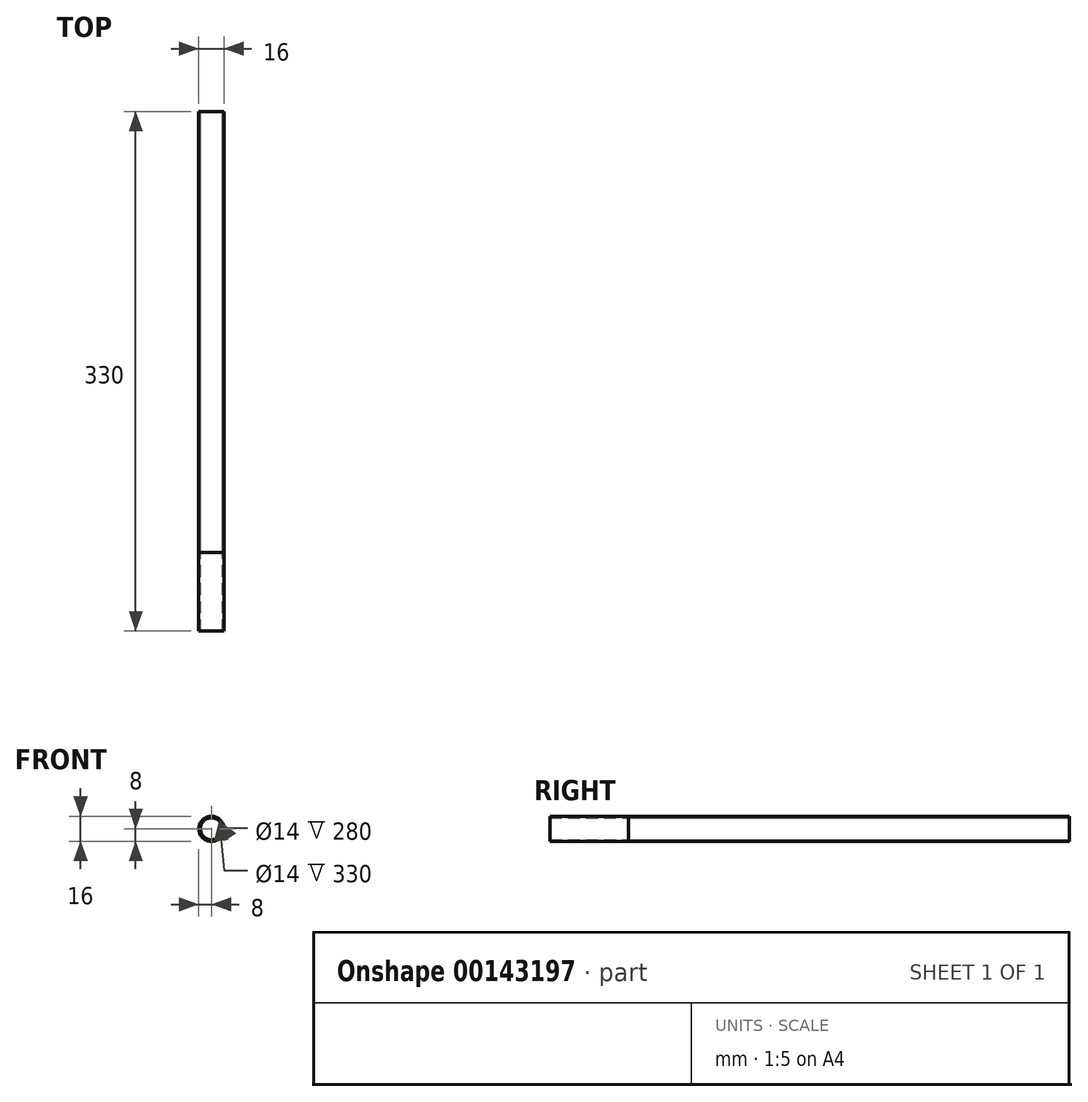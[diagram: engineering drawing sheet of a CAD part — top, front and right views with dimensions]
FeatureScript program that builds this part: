
annotation { "Feature Type Name" : "Feature", "Feature Type Description" : "" }
export const myFeature = defineFeature(function(context is Context, id is Id, definition is map)
    precondition{}
    {
        {
            var Q0;
            Q0=qCreatedBy(makeId("Front.planeOp"),FACE);
            var sketch = newSketch(context, id + "F0", { "sketchPlane" : qUnion([Q0])});
            skCircle(sketch, "E0", {"center": v(0, 0) * mm, "radius": 7 * mm});
            skCircle(sketch, "E1", {"center": v(0, 0) * mm, "radius": 8 * mm});
            skSolve(sketch);
        }
        {
            var Q0;
            Q0=makeQuery(id+"F0.imprint","IMPRINT",FACE,{"disambiguationData":[TD([[makeQuery(id+"F0.imprint","IMPRINT",EDGE,{"derivedFrom":sQuery(id+"F0.wireOp",EDGE,"E0")}),-1.0]])]});
            extrude(context, id + "F1", {"entities" : qUnion([Q0]), "depth" : 330 * mm});
        }
        {
            var Q0;
            Q0=qSketchRegion(id+"F0",true);
            extrude(context, id + "F2", {"entities" : qUnion([Q0]), "depth" : 280 * mm});
        }
    });
